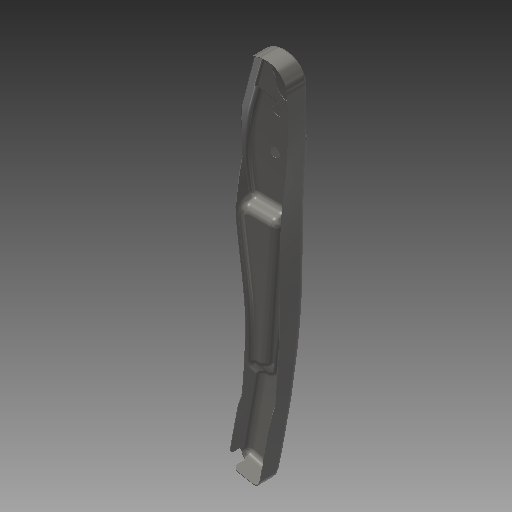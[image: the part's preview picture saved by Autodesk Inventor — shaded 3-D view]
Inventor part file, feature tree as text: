
AUTODESK INVENTOR PART (.ipt)
format: ipt  version: 2019 (Build 230136000, 136)  size: 1,473,536 bytes
history: native  units: mm
features: other x2, plane x1
ambient origin geometry x8: Origin, YZ Plane, XZ Plane, XY Plane, X Axis, Y Axis, Z Axis, Center Point
bodies: Solid1 (feature_tree)
feature tree (3):
  other  "Upper Platform R.ipt"
  plane  "Work Plane3"
  other  "Solid1::Upper Platform R.ipt"
